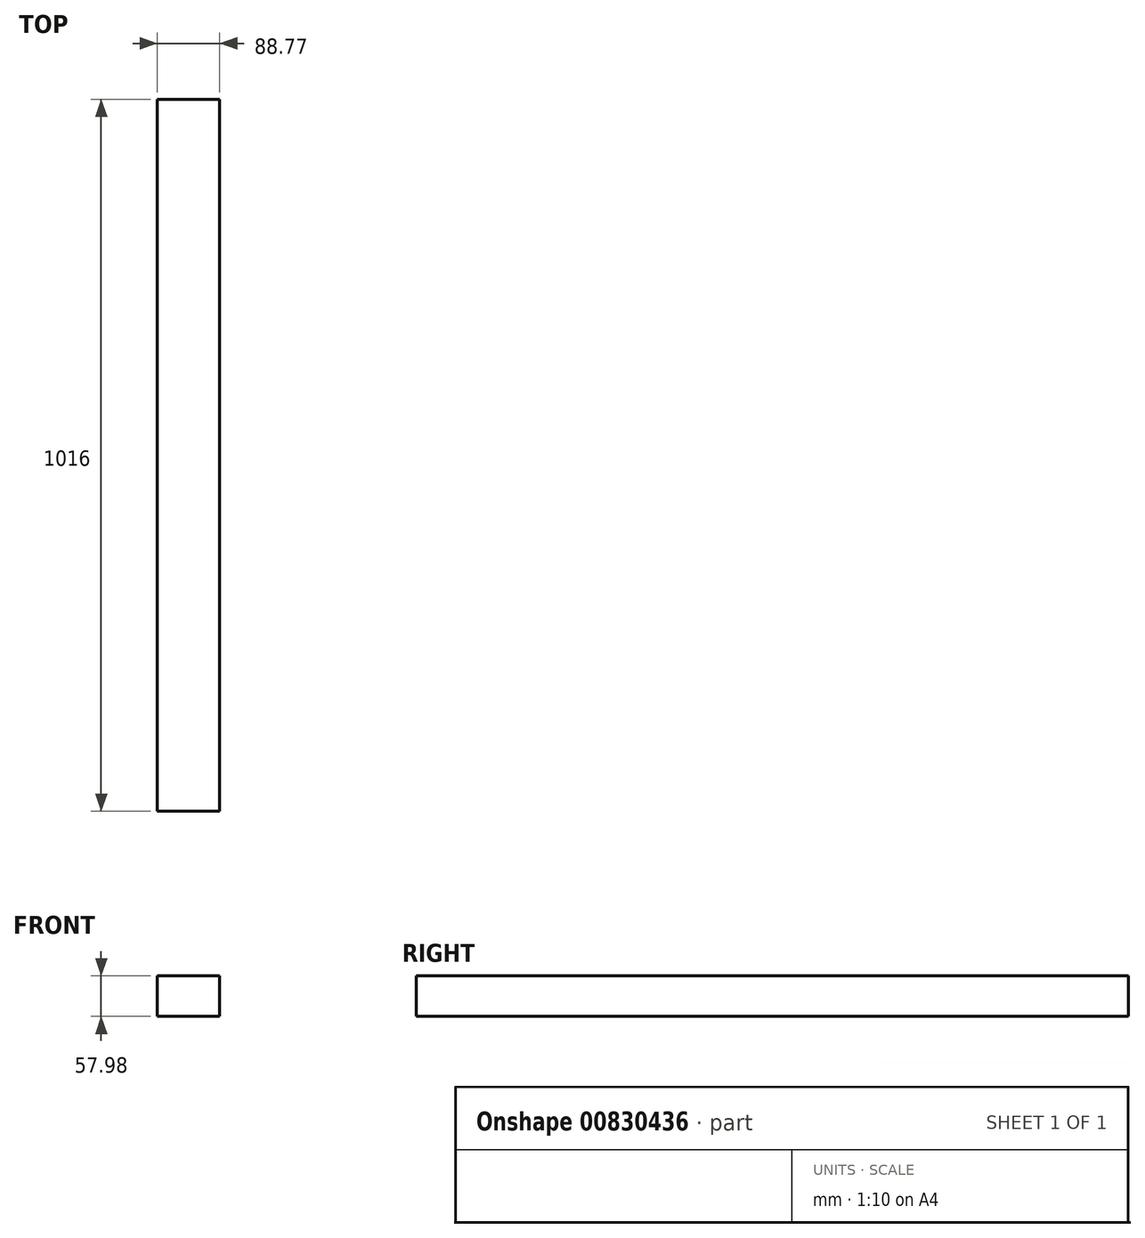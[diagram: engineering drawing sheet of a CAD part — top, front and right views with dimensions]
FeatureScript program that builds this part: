
annotation { "Feature Type Name" : "Feature", "Feature Type Description" : "" }
export const myFeature = defineFeature(function(context is Context, id is Id, definition is map)
    precondition{}
    {
        {
            var Q0;
            Q0=qCreatedBy(makeId("Front.planeOp"),FACE);
            var sketch = newSketch(context, id + "F0", { "sketchPlane" : qUnion([Q0])});
            skLineSegment(sketch, "E0.bottom", {"start": v(0, 0) * mm, "end": v(88.77, 0) * mm});
            skLineSegment(sketch, "E0.top", {"start": v(0, 57.98) * mm, "end": v(88.77, 57.98) * mm});
            skLineSegment(sketch, "E0.left", {"start": v(0, 0) * mm, "end": v(0, 57.98) * mm});
            skLineSegment(sketch, "E0.right", {"start": v(88.77, 0) * mm, "end": v(88.77, 57.98) * mm});
            skSolve(sketch);
        }
        {
            var Q0;
            Q0=makeQuery(id+"F0.imprint","IMPRINT",FACE,{"disambiguationData":[TD([[makeQuery(id+"F0.imprint","IMPRINT",EDGE,{"derivedFrom":sQuery(id+"F0.wireOp",EDGE,"E0.bottom")}),1.0]])]});
            extrude(context, id + "F1", {"entities" : qUnion([Q0]), "depth" : 1016 * mm, "offsetDistance" : 25.4 * mm});
        }
    });
